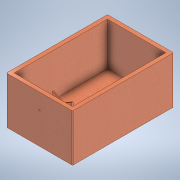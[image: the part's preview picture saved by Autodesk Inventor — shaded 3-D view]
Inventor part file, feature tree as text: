
AUTODESK INVENTOR PART (.ipt)
format: ipt  version: 2022.2 (Build 262287010, 287A)  size: 242,688 bytes
history: native  units: in
note: dims shown in document units (in); Inventor stores cm internally (conversion verified against a paired STEP export)
features: extrude x13, sketch x5, other x1, fillet x1
ambient origin geometry x8: Origin, YZ Plane, XZ Plane, XY Plane, X Axis, Y Axis, Z Axis, Center Point
bodies: Body1 (feature_tree)
feature tree (20):
  other  "Sólido1"
  sketch  "Boceto1"  dims[d0=6.6929in d1=10.2362in]
  extrude  "Extrusión1"  Depth=10.2362in
  extrude  "Extrusión3"  Depth=0.3937in
  sketch  "Boceto4"  dims[d2=4.7638in d3=0.0in d10=0.3937in]
  extrude  "Extrusión4"  Depth=0.3937in
  extrude  "Extrusión5"  Depth=0.8268in TaperAngle=0.0deg
  sketch  "Boceto7"  dims[d11=0.3937in d12=0.0in d15=0.2953in]
  sketch  "Boceto8"  dims[d17=0.0157in d18=0.8268in d19=0.0in]
  extrude  "Extrusión9"  Depth=0.3937in TaperAngle=0.0deg
  sketch  "Boceto9"  dims[d20=0.1181in d21=0.3937in d22=0.0in d23=5.2831in d36=1.9685in d37=3.937in d38=0.3937in d43=1.2547in d44=1.9685in d45=1.9685in d46=0.1575in d47=0.0591in d48=2.7953in d49=0.0in d62=0.1575in d63=0.0in d64=0.1575in d65=0.0in d66=0.1575in d67=0.0in d68=0.1575in d69=0.0in d70=0.1575in d71=0.0in d72=0.1575in d73=0.0in d74=0.0787in d75=0.1181in d76=0.0394in d77=0.0in d98=0.1969in d99=0.0in d100=0.5315in d101=0.2165in d102=0.5315in d103=0.2165in d104=0.5315in d105=0.2165in d106=0.5315in d107=0.2165in d7=0.0197in d8=0.0344in d9=0.0197in d108=0.0197in d109=0.0344in d110=0.0197in d111=0.0344in]
  extrude  "Extrusión11"  Depth=0.0197in
  extrude  "Extrusión12"  Depth=1.9685in
  extrude  "Extrusión13"  Depth=3.937in
  extrude  "Extrusión14"  Depth=0.3937in
  extrude  "Extrusión15"  Depth=0.0197in
  extrude  "Extrusión16"  Depth=1.9685in
  fillet  "Empalme1"  Radius=1.9685in
  extrude  "Extrusión17"  Depth=0.1575in
  extrude  "Extrusión20"  Depth=0.0591in
